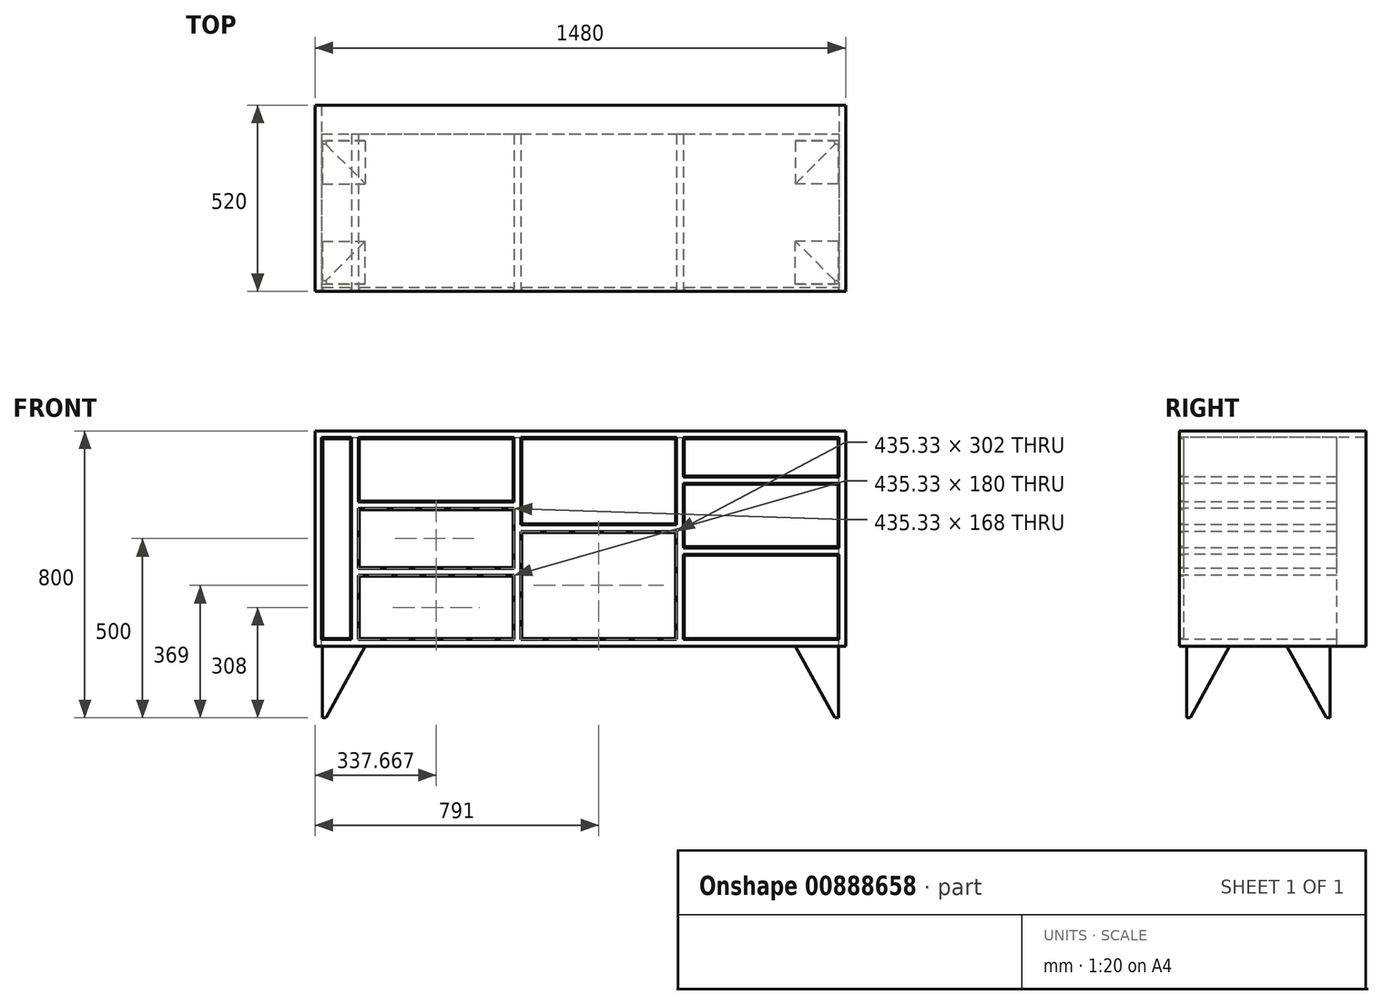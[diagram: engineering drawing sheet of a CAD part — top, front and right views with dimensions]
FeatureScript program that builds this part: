
annotation { "Feature Type Name" : "Feature", "Feature Type Description" : "" }
export const myFeature = defineFeature(function(context is Context, id is Id, definition is map)
    precondition{}
    {
        {
            assignVariable(context, id + "F0", {"name" : "depth", "anyValue" : 520});
        }
        {
            assignVariable(context, id + "F1", {"name" : "hollow_back", "anyValue" : 80});
        }
        {
            var Q0;
            Q0=qCreatedBy(makeId("Front.planeOp"),FACE);
            var sketch = newSketch(context, id + "F2", { "sketchPlane" : qUnion([Q0])});
            skLineSegment(sketch, "E0.bottom", {"start": v(0, 0) * mm, "end": v(1480, 0) * mm});
            skLineSegment(sketch, "E0.top", {"start": v(0, 600) * mm, "end": v(1480, 600) * mm});
            skLineSegment(sketch, "E0.left", {"start": v(0, 0) * mm, "end": v(0, 600) * mm});
            skLineSegment(sketch, "E0.right", {"start": v(1480, 0) * mm, "end": v(1480, 600) * mm});
            skLineSegment(sketch, "E1", {"start": v(120, 0) * mm, "end": v(120, 600) * mm});
            skLineSegment(sketch, "E2.0", {"start": v(102, 0) * mm, "end": v(102, 600) * mm});
            skLineSegment(sketch, "E3.0", {"start": v(18, 0) * mm, "end": v(18, 600) * mm});
            skLineSegment(sketch, "E4", {"start": v(564.33, 0) * mm, "end": v(564.33, 600) * mm});
            skLineSegment(sketch, "E5", {"start": v(1017.67, 0) * mm, "end": v(1017.67, 600) * mm});
            skLineSegment(sketch, "E6.0", {"start": v(573.33, 0) * mm, "end": v(573.33, 600) * mm});
            skLineSegment(sketch, "E7.0", {"start": v(555.33, 0) * mm, "end": v(555.33, 600) * mm});
            skLineSegment(sketch, "E8.0", {"start": v(1026.67, 0) * mm, "end": v(1026.67, 600) * mm});
            skLineSegment(sketch, "E9.0", {"start": v(1008.67, 0) * mm, "end": v(1008.67, 600) * mm});
            skLineSegment(sketch, "E10.0", {"start": v(0, 582) * mm, "end": v(1480, 582) * mm});
            skLineSegment(sketch, "E11.0", {"start": v(1462, 0) * mm, "end": v(1462, 600) * mm});
            skLineSegment(sketch, "E12.0", {"start": v(0, 18) * mm, "end": v(1480, 18) * mm});
            skLineSegment(sketch, "E13.0", {"start": v(111, 0) * mm, "end": v(111, 600) * mm});
            skLineSegment(sketch, "E14.0", {"start": v(1471, 0) * mm, "end": v(1471, 600) * mm});
            skLineSegment(sketch, "E15", {"start": v(573.33, 338) * mm, "end": v(1008.67, 338) * mm});
            skLineSegment(sketch, "E16.0", {"start": v(573.33, 320) * mm, "end": v(1008.67, 320) * mm});
            skLineSegment(sketch, "E17", {"start": v(120, 402) * mm, "end": v(555.33, 402) * mm});
            skLineSegment(sketch, "E18.0", {"start": v(120, 384) * mm, "end": v(555.33, 384) * mm});
            skLineSegment(sketch, "E19", {"start": v(120, 216) * mm, "end": v(555.33, 216) * mm});
            skLineSegment(sketch, "E20.0", {"start": v(120, 198) * mm, "end": v(555.33, 198) * mm});
            skLineSegment(sketch, "E21", {"start": v(1026.67, 472) * mm, "end": v(1462, 472) * mm});
            skLineSegment(sketch, "E22.0", {"start": v(1026.67, 454) * mm, "end": v(1462, 454) * mm});
            skLineSegment(sketch, "E23", {"start": v(1026.67, 274) * mm, "end": v(1462, 274) * mm});
            skLineSegment(sketch, "E24.0", {"start": v(1026.67, 256) * mm, "end": v(1462, 256) * mm});
            skSolve(sketch);
        }
        {
            var Q0;
            {var subQ0=sQuery(id+"F2.wireOp",EDGE,"E10.0");var subQ1=sQuery(id+"F2.wireOp",EDGE,"E0.left");var subQ2=makeQuery(id+"F2.imprint","INTERSECT",VERTEX,{"derivedFrom":[subQ1,subQ0]});Q0=makeQuery(id+"F2.imprint","IMPRINT",FACE,{"disambiguationData":[TD([[makeQuery(id+"F2.imprint","IMPRINT",EDGE,{"disambiguationData":[TD([[subQ2,1.0]])],"derivedFrom":subQ1}),-1.0]])]});}
            var Q1;
            {var subQ0=sQuery(id+"F2.wireOp",EDGE,"E0.left");var subQ1=sQuery(id+"F2.wireOp",EDGE,"E0.top");var subQ2=makeQuery(id+"F2.imprint","INTERSECT",VERTEX,{"derivedFrom":[subQ1,subQ0]});Q1=makeQuery(id+"F2.imprint","IMPRINT",FACE,{"disambiguationData":[TD([[makeQuery(id+"F2.imprint","IMPRINT",EDGE,{"disambiguationData":[TD([[subQ2,-1.0]])],"derivedFrom":subQ1}),-1.0]])]});}
            var Q2;
            {var subQ0=sQuery(id+"F2.wireOp",EDGE,"E2.0");var subQ1=sQuery(id+"F2.wireOp",EDGE,"E0.top");var subQ2=makeQuery(id+"F2.imprint","INTERSECT",VERTEX,{"derivedFrom":[subQ1,subQ0]});Q2=makeQuery(id+"F2.imprint","IMPRINT",FACE,{"disambiguationData":[TD([[makeQuery(id+"F2.imprint","IMPRINT",EDGE,{"disambiguationData":[TD([[subQ2,1.0]])],"derivedFrom":subQ1}),-1.0]])]});}
            var Q3;
            {var subQ0=sQuery(id+"F2.wireOp",EDGE,"E1");var subQ1=sQuery(id+"F2.wireOp",EDGE,"E0.top");var subQ2=makeQuery(id+"F2.imprint","INTERSECT",VERTEX,{"derivedFrom":[subQ1,subQ0]});Q3=makeQuery(id+"F2.imprint","IMPRINT",FACE,{"disambiguationData":[TD([[makeQuery(id+"F2.imprint","IMPRINT",EDGE,{"disambiguationData":[TD([[subQ2,1.0]])],"derivedFrom":subQ1}),-1.0]])]});}
            var Q4;
            {var subQ0=sQuery(id+"F2.wireOp",EDGE,"E1");var subQ1=sQuery(id+"F2.wireOp",EDGE,"E0.top");var subQ2=makeQuery(id+"F2.imprint","INTERSECT",VERTEX,{"derivedFrom":[subQ1,subQ0]});Q4=makeQuery(id+"F2.imprint","IMPRINT",FACE,{"disambiguationData":[TD([[makeQuery(id+"F2.imprint","IMPRINT",EDGE,{"disambiguationData":[TD([[subQ2,-1.0]])],"derivedFrom":subQ1}),-1.0]])]});}
            var Q5;
            {var subQ0=sQuery(id+"F2.wireOp",EDGE,"E4");var subQ1=sQuery(id+"F2.wireOp",EDGE,"E0.top");var subQ2=makeQuery(id+"F2.imprint","INTERSECT",VERTEX,{"derivedFrom":[subQ1,subQ0]});Q5=makeQuery(id+"F2.imprint","IMPRINT",FACE,{"disambiguationData":[TD([[makeQuery(id+"F2.imprint","IMPRINT",EDGE,{"disambiguationData":[TD([[subQ2,1.0]])],"derivedFrom":subQ1}),-1.0]])]});}
            var Q6;
            {var subQ0=sQuery(id+"F2.wireOp",EDGE,"E4");var subQ1=sQuery(id+"F2.wireOp",EDGE,"E0.top");var subQ2=makeQuery(id+"F2.imprint","INTERSECT",VERTEX,{"derivedFrom":[subQ1,subQ0]});Q6=makeQuery(id+"F2.imprint","IMPRINT",FACE,{"disambiguationData":[TD([[makeQuery(id+"F2.imprint","IMPRINT",EDGE,{"disambiguationData":[TD([[subQ2,-1.0]])],"derivedFrom":subQ1}),-1.0]])]});}
            var Q7;
            {var subQ0=sQuery(id+"F2.wireOp",EDGE,"E6.0");var subQ1=sQuery(id+"F2.wireOp",EDGE,"E0.top");var subQ2=makeQuery(id+"F2.imprint","INTERSECT",VERTEX,{"derivedFrom":[subQ1,subQ0]});Q7=makeQuery(id+"F2.imprint","IMPRINT",FACE,{"disambiguationData":[TD([[makeQuery(id+"F2.imprint","IMPRINT",EDGE,{"disambiguationData":[TD([[subQ2,-1.0]])],"derivedFrom":subQ1}),-1.0]])]});}
            var Q8;
            {var subQ0=sQuery(id+"F2.wireOp",EDGE,"E5");var subQ1=sQuery(id+"F2.wireOp",EDGE,"E0.top");var subQ2=makeQuery(id+"F2.imprint","INTERSECT",VERTEX,{"derivedFrom":[subQ1,subQ0]});Q8=makeQuery(id+"F2.imprint","IMPRINT",FACE,{"disambiguationData":[TD([[makeQuery(id+"F2.imprint","IMPRINT",EDGE,{"disambiguationData":[TD([[subQ2,1.0]])],"derivedFrom":subQ1}),-1.0]])]});}
            var Q9;
            {var subQ0=sQuery(id+"F2.wireOp",EDGE,"E5");var subQ1=sQuery(id+"F2.wireOp",EDGE,"E0.top");var subQ2=makeQuery(id+"F2.imprint","INTERSECT",VERTEX,{"derivedFrom":[subQ1,subQ0]});Q9=makeQuery(id+"F2.imprint","IMPRINT",FACE,{"disambiguationData":[TD([[makeQuery(id+"F2.imprint","IMPRINT",EDGE,{"disambiguationData":[TD([[subQ2,-1.0]])],"derivedFrom":subQ1}),-1.0]])]});}
            var Q10;
            {var subQ0=sQuery(id+"F2.wireOp",EDGE,"E8.0");var subQ1=sQuery(id+"F2.wireOp",EDGE,"E0.top");var subQ2=makeQuery(id+"F2.imprint","INTERSECT",VERTEX,{"derivedFrom":[subQ1,subQ0]});Q10=makeQuery(id+"F2.imprint","IMPRINT",FACE,{"disambiguationData":[TD([[makeQuery(id+"F2.imprint","IMPRINT",EDGE,{"disambiguationData":[TD([[subQ2,-1.0]])],"derivedFrom":subQ1}),-1.0]])]});}
            var Q11;
            {var subQ0=sQuery(id+"F2.wireOp",EDGE,"E0.right");var subQ1=sQuery(id+"F2.wireOp",EDGE,"E0.top");var subQ2=makeQuery(id+"F2.imprint","INTERSECT",VERTEX,{"derivedFrom":[subQ1,subQ0]});Q11=makeQuery(id+"F2.imprint","IMPRINT",FACE,{"disambiguationData":[TD([[makeQuery(id+"F2.imprint","IMPRINT",EDGE,{"disambiguationData":[TD([[subQ2,1.0]])],"derivedFrom":subQ1}),-1.0]])]});}
            var Q12;
            {var subQ0=sQuery(id+"F2.wireOp",EDGE,"E10.0");var subQ1=sQuery(id+"F2.wireOp",EDGE,"E0.right");var subQ2=makeQuery(id+"F2.imprint","INTERSECT",VERTEX,{"derivedFrom":[subQ1,subQ0]});Q12=makeQuery(id+"F2.imprint","IMPRINT",FACE,{"disambiguationData":[TD([[makeQuery(id+"F2.imprint","IMPRINT",EDGE,{"disambiguationData":[TD([[subQ2,1.0]])],"derivedFrom":subQ1}),1.0]])]});}
            var Q13;
            {var subQ0=sQuery(id+"F2.wireOp",EDGE,"E0.right");var subQ1=sQuery(id+"F2.wireOp",EDGE,"E0.bottom");var subQ2=makeQuery(id+"F2.imprint","INTERSECT",VERTEX,{"derivedFrom":[subQ1,subQ0]});Q13=makeQuery(id+"F2.imprint","IMPRINT",FACE,{"disambiguationData":[TD([[makeQuery(id+"F2.imprint","IMPRINT",EDGE,{"disambiguationData":[TD([[subQ2,1.0]])],"derivedFrom":subQ1}),1.0]])]});}
            var Q14;
            {var subQ0=sQuery(id+"F2.wireOp",EDGE,"E0.left");var subQ1=sQuery(id+"F2.wireOp",EDGE,"E0.bottom");var subQ2=makeQuery(id+"F2.imprint","INTERSECT",VERTEX,{"derivedFrom":[subQ1,subQ0]});Q14=makeQuery(id+"F2.imprint","IMPRINT",FACE,{"disambiguationData":[TD([[makeQuery(id+"F2.imprint","IMPRINT",EDGE,{"disambiguationData":[TD([[subQ2,-1.0]])],"derivedFrom":subQ1}),1.0]])]});}
            var Q15;
            {var subQ0=sQuery(id+"F2.wireOp",EDGE,"E2.0");var subQ1=sQuery(id+"F2.wireOp",EDGE,"E0.top");var subQ2=makeQuery(id+"F2.imprint","INTERSECT",VERTEX,{"derivedFrom":[subQ1,subQ0]});Q15=makeQuery(id+"F2.imprint","IMPRINT",FACE,{"disambiguationData":[TD([[makeQuery(id+"F2.imprint","IMPRINT",EDGE,{"disambiguationData":[TD([[subQ2,-1.0]])],"derivedFrom":subQ1}),-1.0]])]});}
            var Q16;
            {var subQ0=sQuery(id+"F2.wireOp",EDGE,"E11.0");var subQ1=sQuery(id+"F2.wireOp",EDGE,"E0.top");var subQ2=makeQuery(id+"F2.imprint","INTERSECT",VERTEX,{"derivedFrom":[subQ1,subQ0]});Q16=makeQuery(id+"F2.imprint","IMPRINT",FACE,{"disambiguationData":[TD([[makeQuery(id+"F2.imprint","IMPRINT",EDGE,{"disambiguationData":[TD([[subQ2,-1.0]])],"derivedFrom":subQ1}),-1.0]])]});}
            var Q17;
            {var subQ0=sQuery(id+"F2.wireOp",EDGE,"E11.0");var subQ1=sQuery(id+"F2.wireOp",EDGE,"E10.0");var subQ2=makeQuery(id+"F2.imprint","INTERSECT",VERTEX,{"derivedFrom":[subQ1,subQ0]});Q17=makeQuery(id+"F2.imprint","IMPRINT",FACE,{"disambiguationData":[TD([[makeQuery(id+"F2.imprint","IMPRINT",EDGE,{"disambiguationData":[TD([[subQ2,-1.0]])],"derivedFrom":subQ1}),-1.0]])]});}
            var Q18;
            {var subQ0=sQuery(id+"F2.wireOp",EDGE,"E11.0");var subQ1=sQuery(id+"F2.wireOp",EDGE,"E0.bottom");var subQ2=makeQuery(id+"F2.imprint","INTERSECT",VERTEX,{"derivedFrom":[subQ1,subQ0]});Q18=makeQuery(id+"F2.imprint","IMPRINT",FACE,{"disambiguationData":[TD([[makeQuery(id+"F2.imprint","IMPRINT",EDGE,{"disambiguationData":[TD([[subQ2,-1.0]])],"derivedFrom":subQ1}),1.0]])]});}
            extrude(context, id + "F3", {"entities" : qUnion([Q0, Q1, Q2, Q3, Q4, Q5, Q6, Q7, Q8, Q9, Q10, Q11, Q12, Q13, Q14, Q15, Q16, Q17, Q18]), "oppositeDirection" : true, "depth" : (getVariable(context, 'depth')) * mm, "offsetDistance" : 25 * mm});
        }
        {
            var Q0;
            {var subQ0=sQuery(id+"F2.wireOp",EDGE,"E8.0");var subQ1=sQuery(id+"F2.wireOp",EDGE,"E0.bottom");var subQ2=makeQuery(id+"F2.imprint","INTERSECT",VERTEX,{"derivedFrom":[subQ1,subQ0]});Q0=makeQuery(id+"F2.imprint","IMPRINT",FACE,{"disambiguationData":[TD([[makeQuery(id+"F2.imprint","IMPRINT",EDGE,{"disambiguationData":[TD([[subQ2,-1.0]])],"derivedFrom":subQ1}),1.0]])]});}
            var Q1;
            {var subQ0=sQuery(id+"F2.wireOp",EDGE,"E5");var subQ1=sQuery(id+"F2.wireOp",EDGE,"E0.bottom");var subQ2=makeQuery(id+"F2.imprint","INTERSECT",VERTEX,{"derivedFrom":[subQ1,subQ0]});Q1=makeQuery(id+"F2.imprint","IMPRINT",FACE,{"disambiguationData":[TD([[makeQuery(id+"F2.imprint","IMPRINT",EDGE,{"disambiguationData":[TD([[subQ2,-1.0]])],"derivedFrom":subQ1}),1.0]])]});}
            var Q2;
            {var subQ0=sQuery(id+"F2.wireOp",EDGE,"E5");var subQ1=sQuery(id+"F2.wireOp",EDGE,"E0.bottom");var subQ2=makeQuery(id+"F2.imprint","INTERSECT",VERTEX,{"derivedFrom":[subQ1,subQ0]});Q2=makeQuery(id+"F2.imprint","IMPRINT",FACE,{"disambiguationData":[TD([[makeQuery(id+"F2.imprint","IMPRINT",EDGE,{"disambiguationData":[TD([[subQ2,1.0]])],"derivedFrom":subQ1}),1.0]])]});}
            var Q3;
            {var subQ0=sQuery(id+"F2.wireOp",EDGE,"E6.0");var subQ1=sQuery(id+"F2.wireOp",EDGE,"E0.bottom");var subQ2=makeQuery(id+"F2.imprint","INTERSECT",VERTEX,{"derivedFrom":[subQ1,subQ0]});Q3=makeQuery(id+"F2.imprint","IMPRINT",FACE,{"disambiguationData":[TD([[makeQuery(id+"F2.imprint","IMPRINT",EDGE,{"disambiguationData":[TD([[subQ2,-1.0]])],"derivedFrom":subQ1}),1.0]])]});}
            var Q4;
            {var subQ0=sQuery(id+"F2.wireOp",EDGE,"E4");var subQ1=sQuery(id+"F2.wireOp",EDGE,"E0.bottom");var subQ2=makeQuery(id+"F2.imprint","INTERSECT",VERTEX,{"derivedFrom":[subQ1,subQ0]});Q4=makeQuery(id+"F2.imprint","IMPRINT",FACE,{"disambiguationData":[TD([[makeQuery(id+"F2.imprint","IMPRINT",EDGE,{"disambiguationData":[TD([[subQ2,-1.0]])],"derivedFrom":subQ1}),1.0]])]});}
            var Q5;
            {var subQ0=sQuery(id+"F2.wireOp",EDGE,"E4");var subQ1=sQuery(id+"F2.wireOp",EDGE,"E0.bottom");var subQ2=makeQuery(id+"F2.imprint","INTERSECT",VERTEX,{"derivedFrom":[subQ1,subQ0]});Q5=makeQuery(id+"F2.imprint","IMPRINT",FACE,{"disambiguationData":[TD([[makeQuery(id+"F2.imprint","IMPRINT",EDGE,{"disambiguationData":[TD([[subQ2,1.0]])],"derivedFrom":subQ1}),1.0]])]});}
            var Q6;
            {var subQ0=sQuery(id+"F2.wireOp",EDGE,"E1");var subQ1=sQuery(id+"F2.wireOp",EDGE,"E0.bottom");var subQ2=makeQuery(id+"F2.imprint","INTERSECT",VERTEX,{"derivedFrom":[subQ1,subQ0]});Q6=makeQuery(id+"F2.imprint","IMPRINT",FACE,{"disambiguationData":[TD([[makeQuery(id+"F2.imprint","IMPRINT",EDGE,{"disambiguationData":[TD([[subQ2,-1.0]])],"derivedFrom":subQ1}),1.0]])]});}
            var Q7;
            {var subQ0=sQuery(id+"F2.wireOp",EDGE,"E1");var subQ1=sQuery(id+"F2.wireOp",EDGE,"E0.bottom");var subQ2=makeQuery(id+"F2.imprint","INTERSECT",VERTEX,{"derivedFrom":[subQ1,subQ0]});Q7=makeQuery(id+"F2.imprint","IMPRINT",FACE,{"disambiguationData":[TD([[makeQuery(id+"F2.imprint","IMPRINT",EDGE,{"disambiguationData":[TD([[subQ2,1.0]])],"derivedFrom":subQ1}),1.0]])]});}
            var Q8;
            {var subQ0=sQuery(id+"F2.wireOp",EDGE,"E2.0");var subQ1=sQuery(id+"F2.wireOp",EDGE,"E0.bottom");var subQ2=makeQuery(id+"F2.imprint","INTERSECT",VERTEX,{"derivedFrom":[subQ1,subQ0]});Q8=makeQuery(id+"F2.imprint","IMPRINT",FACE,{"disambiguationData":[TD([[makeQuery(id+"F2.imprint","IMPRINT",EDGE,{"disambiguationData":[TD([[subQ2,1.0]])],"derivedFrom":subQ1}),1.0]])]});}
            var Q9;
            {var subQ0=sQuery(id+"F2.wireOp",EDGE,"E12.0");var subQ1=sQuery(id+"F2.wireOp",EDGE,"E1");var subQ2=makeQuery(id+"F2.imprint","INTERSECT",VERTEX,{"derivedFrom":[subQ1,subQ0]});Q9=makeQuery(id+"F2.imprint","IMPRINT",FACE,{"disambiguationData":[TD([[makeQuery(id+"F2.imprint","IMPRINT",EDGE,{"disambiguationData":[TD([[subQ2,-1.0]])],"derivedFrom":subQ1}),1.0]])]});}
            var Q10;
            {var subQ0=sQuery(id+"F2.wireOp",EDGE,"E12.0");var subQ1=sQuery(id+"F2.wireOp",EDGE,"E4");var subQ2=makeQuery(id+"F2.imprint","INTERSECT",VERTEX,{"derivedFrom":[subQ1,subQ0]});Q10=makeQuery(id+"F2.imprint","IMPRINT",FACE,{"disambiguationData":[TD([[makeQuery(id+"F2.imprint","IMPRINT",EDGE,{"disambiguationData":[TD([[subQ2,-1.0]])],"derivedFrom":subQ1}),1.0]])]});}
            var Q11;
            {var subQ0=sQuery(id+"F2.wireOp",EDGE,"E12.0");var subQ1=sQuery(id+"F2.wireOp",EDGE,"E4");var subQ2=makeQuery(id+"F2.imprint","INTERSECT",VERTEX,{"derivedFrom":[subQ1,subQ0]});Q11=makeQuery(id+"F2.imprint","IMPRINT",FACE,{"disambiguationData":[TD([[makeQuery(id+"F2.imprint","IMPRINT",EDGE,{"disambiguationData":[TD([[subQ2,-1.0]])],"derivedFrom":subQ1}),-1.0]])]});}
            var Q12;
            {var subQ0=sQuery(id+"F2.wireOp",EDGE,"E12.0");var subQ1=sQuery(id+"F2.wireOp",EDGE,"E5");var subQ2=makeQuery(id+"F2.imprint","INTERSECT",VERTEX,{"derivedFrom":[subQ1,subQ0]});Q12=makeQuery(id+"F2.imprint","IMPRINT",FACE,{"disambiguationData":[TD([[makeQuery(id+"F2.imprint","IMPRINT",EDGE,{"disambiguationData":[TD([[subQ2,-1.0]])],"derivedFrom":subQ1}),1.0]])]});}
            var Q13;
            {var subQ0=sQuery(id+"F2.wireOp",EDGE,"E12.0");var subQ1=sQuery(id+"F2.wireOp",EDGE,"E5");var subQ2=makeQuery(id+"F2.imprint","INTERSECT",VERTEX,{"derivedFrom":[subQ1,subQ0]});Q13=makeQuery(id+"F2.imprint","IMPRINT",FACE,{"disambiguationData":[TD([[makeQuery(id+"F2.imprint","IMPRINT",EDGE,{"disambiguationData":[TD([[subQ2,-1.0]])],"derivedFrom":subQ1}),-1.0]])]});}
            var Q14;
            {var subQ0=sQuery(id+"F2.wireOp",EDGE,"E2.0");var subQ1=sQuery(id+"F2.wireOp",EDGE,"E0.bottom");var subQ2=makeQuery(id+"F2.imprint","INTERSECT",VERTEX,{"derivedFrom":[subQ1,subQ0]});Q14=makeQuery(id+"F2.imprint","IMPRINT",FACE,{"disambiguationData":[TD([[makeQuery(id+"F2.imprint","IMPRINT",EDGE,{"disambiguationData":[TD([[subQ2,-1.0]])],"derivedFrom":subQ1}),1.0]])]});}
            var Q15;
            {var subQ0=sQuery(id+"F2.wireOp",EDGE,"E12.0");var subQ1=sQuery(id+"F2.wireOp",EDGE,"E2.0");var subQ2=makeQuery(id+"F2.imprint","INTERSECT",VERTEX,{"derivedFrom":[subQ1,subQ0]});Q15=makeQuery(id+"F2.imprint","IMPRINT",FACE,{"disambiguationData":[TD([[makeQuery(id+"F2.imprint","IMPRINT",EDGE,{"disambiguationData":[TD([[subQ2,-1.0]])],"derivedFrom":subQ1}),-1.0]])]});}
            var Q16;
            {var subQ0=sQuery(id+"F2.wireOp",EDGE,"E17");Q16=makeQuery(id+"F2.imprint","IMPRINT",FACE,{"disambiguationData":[TD([[makeQuery(id+"F2.imprint","IMPRINT",EDGE,{"derivedFrom":subQ0}),-1.0]])]});}
            var Q17;
            {var subQ0=sQuery(id+"F2.wireOp",EDGE,"E19");Q17=makeQuery(id+"F2.imprint","IMPRINT",FACE,{"disambiguationData":[TD([[makeQuery(id+"F2.imprint","IMPRINT",EDGE,{"derivedFrom":subQ0}),-1.0]])]});}
            var Q18;
            {var subQ0=sQuery(id+"F2.wireOp",EDGE,"E15");Q18=makeQuery(id+"F2.imprint","IMPRINT",FACE,{"disambiguationData":[TD([[makeQuery(id+"F2.imprint","IMPRINT",EDGE,{"derivedFrom":subQ0}),-1.0]])]});}
            var Q19;
            {var subQ0=sQuery(id+"F2.wireOp",EDGE,"E21");Q19=makeQuery(id+"F2.imprint","IMPRINT",FACE,{"disambiguationData":[TD([[makeQuery(id+"F2.imprint","IMPRINT",EDGE,{"derivedFrom":subQ0}),-1.0]])]});}
            var Q20;
            {var subQ0=sQuery(id+"F2.wireOp",EDGE,"E23");Q20=makeQuery(id+"F2.imprint","IMPRINT",FACE,{"disambiguationData":[TD([[makeQuery(id+"F2.imprint","IMPRINT",EDGE,{"derivedFrom":subQ0}),-1.0]])]});}
            extrude(context, id + "F4", {"entities" : qUnion([Q0, Q1, Q2, Q3, Q4, Q5, Q6, Q7, Q8, Q9, Q10, Q11, Q12, Q13, Q14, Q15, Q16, Q17, Q18, Q19, Q20]), "operationType" : NewBodyOperationType.ADD, "oppositeDirection" : true, "depth" : (getVariable(context, 'depth') - getVariable(context, 'hollow_back')) * mm, "offsetDistance" : 25 * mm});
        }
        {
            var Q0;
            Q0=qCreatedBy(makeId("Front.planeOp"),FACE);
            var sketch = newSketch(context, id + "F5", { "sketchPlane" : qUnion([Q0])});
            skLineSegment(sketch, "E25.0", {"start": v(21, 0) * mm, "end": v(21, 600) * mm});
            skLineSegment(sketch, "E26.0", {"start": v(0, 21) * mm, "end": v(1480, 21) * mm});
            skLineSegment(sketch, "E27.0", {"start": v(99, 0) * mm, "end": v(99, 600) * mm});
            skLineSegment(sketch, "E28.0", {"start": v(0, 579) * mm, "end": v(1480, 579) * mm});
            skLineSegment(sketch, "E29.0", {"start": v(123, 0) * mm, "end": v(123, 600) * mm});
            skLineSegment(sketch, "E30.0", {"start": v(552.33, 0) * mm, "end": v(552.33, 600) * mm});
            skLineSegment(sketch, "E31.0", {"start": v(120, 405) * mm, "end": v(555.33, 405) * mm});
            skLineSegment(sketch, "E32.0", {"start": v(120, 381) * mm, "end": v(555.33, 381) * mm});
            skLineSegment(sketch, "E33.0", {"start": v(120, 219) * mm, "end": v(555.33, 219) * mm});
            skLineSegment(sketch, "E34.0", {"start": v(120, 195) * mm, "end": v(555.33, 195) * mm});
            skLineSegment(sketch, "E35.0", {"start": v(576.33, 0) * mm, "end": v(576.33, 600) * mm});
            skLineSegment(sketch, "E36.0", {"start": v(1005.67, 0) * mm, "end": v(1005.67, 600) * mm});
            skLineSegment(sketch, "E37.0", {"start": v(573.33, 341) * mm, "end": v(1008.67, 341) * mm});
            skLineSegment(sketch, "E38.0", {"start": v(573.33, 317) * mm, "end": v(1008.67, 317) * mm});
            skLineSegment(sketch, "E39.0", {"start": v(1029.67, 0) * mm, "end": v(1029.67, 600) * mm});
            skLineSegment(sketch, "E40.0", {"start": v(1459, 0) * mm, "end": v(1459, 600) * mm});
            skLineSegment(sketch, "E41.0", {"start": v(1026.67, 475) * mm, "end": v(1462, 475) * mm});
            skLineSegment(sketch, "E42.0", {"start": v(1026.67, 451) * mm, "end": v(1462, 451) * mm});
            skLineSegment(sketch, "E43.0", {"start": v(1026.67, 277) * mm, "end": v(1462, 277) * mm});
            skLineSegment(sketch, "E44.0", {"start": v(1026.67, 253) * mm, "end": v(1462, 253) * mm});
            skSolve(sketch);
        }
        {
            var Q0;
            {var subQ0=sQuery(id+"F5.wireOp",EDGE,"E26.0");var subQ1=sQuery(id+"F5.wireOp",EDGE,"E25.0");var subQ2=makeQuery(id+"F5.imprint","INTERSECT",VERTEX,{"derivedFrom":[subQ1,subQ0]});Q0=makeQuery(id+"F5.imprint","IMPRINT",FACE,{"disambiguationData":[TD([[makeQuery(id+"F5.imprint","IMPRINT",EDGE,{"disambiguationData":[TD([[subQ2,-1.0]])],"derivedFrom":subQ1}),-1.0]])]});}
            var Q1;
            {var subQ0=sQuery(id+"F5.wireOp",EDGE,"E30.0");var subQ1=sQuery(id+"F5.wireOp",EDGE,"E28.0");var subQ2=makeQuery(id+"F5.imprint","INTERSECT",VERTEX,{"derivedFrom":[subQ1,subQ0]});Q1=makeQuery(id+"F5.imprint","IMPRINT",FACE,{"disambiguationData":[TD([[makeQuery(id+"F5.imprint","IMPRINT",EDGE,{"disambiguationData":[TD([[subQ2,1.0]])],"derivedFrom":subQ1}),-1.0]])]});}
            var Q2;
            {var subQ0=sQuery(id+"F5.wireOp",EDGE,"E33.0");var subQ1=sQuery(id+"F5.wireOp",EDGE,"E29.0");var subQ2=makeQuery(id+"F5.imprint","INTERSECT",VERTEX,{"derivedFrom":[subQ1,subQ0]});Q2=makeQuery(id+"F5.imprint","IMPRINT",FACE,{"disambiguationData":[TD([[makeQuery(id+"F5.imprint","IMPRINT",EDGE,{"disambiguationData":[TD([[subQ2,-1.0]])],"derivedFrom":subQ1}),-1.0]])]});}
            var Q3;
            {var subQ0=sQuery(id+"F5.wireOp",EDGE,"E29.0");var subQ1=sQuery(id+"F5.wireOp",EDGE,"E26.0");var subQ2=makeQuery(id+"F5.imprint","INTERSECT",VERTEX,{"derivedFrom":[subQ1,subQ0]});Q3=makeQuery(id+"F5.imprint","IMPRINT",FACE,{"disambiguationData":[TD([[makeQuery(id+"F5.imprint","IMPRINT",EDGE,{"disambiguationData":[TD([[subQ2,-1.0]])],"derivedFrom":subQ1}),1.0]])]});}
            var Q4;
            {var subQ0=sQuery(id+"F5.wireOp",EDGE,"E36.0");var subQ1=sQuery(id+"F5.wireOp",EDGE,"E28.0");var subQ2=makeQuery(id+"F5.imprint","INTERSECT",VERTEX,{"derivedFrom":[subQ1,subQ0]});Q4=makeQuery(id+"F5.imprint","IMPRINT",FACE,{"disambiguationData":[TD([[makeQuery(id+"F5.imprint","IMPRINT",EDGE,{"disambiguationData":[TD([[subQ2,1.0]])],"derivedFrom":subQ1}),-1.0]])]});}
            var Q5;
            {var subQ0=sQuery(id+"F5.wireOp",EDGE,"E36.0");var subQ1=sQuery(id+"F5.wireOp",EDGE,"E26.0");var subQ2=makeQuery(id+"F5.imprint","INTERSECT",VERTEX,{"derivedFrom":[subQ1,subQ0]});Q5=makeQuery(id+"F5.imprint","IMPRINT",FACE,{"disambiguationData":[TD([[makeQuery(id+"F5.imprint","IMPRINT",EDGE,{"disambiguationData":[TD([[subQ2,1.0]])],"derivedFrom":subQ1}),1.0]])]});}
            var Q6;
            {var subQ0=sQuery(id+"F5.wireOp",EDGE,"E40.0");var subQ1=sQuery(id+"F5.wireOp",EDGE,"E26.0");var subQ2=makeQuery(id+"F5.imprint","INTERSECT",VERTEX,{"derivedFrom":[subQ1,subQ0]});Q6=makeQuery(id+"F5.imprint","IMPRINT",FACE,{"disambiguationData":[TD([[makeQuery(id+"F5.imprint","IMPRINT",EDGE,{"disambiguationData":[TD([[subQ2,1.0]])],"derivedFrom":subQ1}),1.0]])]});}
            var Q7;
            {var subQ0=sQuery(id+"F5.wireOp",EDGE,"E43.0");var subQ1=sQuery(id+"F5.wireOp",EDGE,"E39.0");var subQ2=makeQuery(id+"F5.imprint","INTERSECT",VERTEX,{"derivedFrom":[subQ1,subQ0]});Q7=makeQuery(id+"F5.imprint","IMPRINT",FACE,{"disambiguationData":[TD([[makeQuery(id+"F5.imprint","IMPRINT",EDGE,{"disambiguationData":[TD([[subQ2,-1.0]])],"derivedFrom":subQ1}),-1.0]])]});}
            var Q8;
            {var subQ0=sQuery(id+"F5.wireOp",EDGE,"E40.0");var subQ1=sQuery(id+"F5.wireOp",EDGE,"E28.0");var subQ2=makeQuery(id+"F5.imprint","INTERSECT",VERTEX,{"derivedFrom":[subQ1,subQ0]});Q8=makeQuery(id+"F5.imprint","IMPRINT",FACE,{"disambiguationData":[TD([[makeQuery(id+"F5.imprint","IMPRINT",EDGE,{"disambiguationData":[TD([[subQ2,1.0]])],"derivedFrom":subQ1}),-1.0]])]});}
            extrude(context, id + "F6", {"entities" : qUnion([Q0, Q1, Q2, Q3, Q4, Q5, Q6, Q7, Q8]), "operationType" : NewBodyOperationType.ADD, "oppositeDirection" : true, "depth" : 12 * mm, "offsetDistance" : 25 * mm});
        }
        {
            var Q0;
            {var subQ0=sQuery(id+"F2.wireOp",EDGE,"E0.bottom");Q0=makeQuery(id+"F4.boolean.opBoolean","MERGE",FACE,{"derivedFrom":[makeQuery(id+"F3.opExtrude","SWEPT_FACE",FACE,{"disambiguationData":[OSD([subQ0]),TDD([makeQuery(id+"F2.imprint","IMPRINT",EDGE,{"disambiguationData":[TD([[makeQuery(id+"F2.imprint","INTERSECT",VERTEX,{"derivedFrom":[subQ0,sQuery(id+"F2.wireOp",EDGE,"E0.left")]}),-1.0]])],"derivedFrom":subQ0})])]}),makeQuery(id+"F3.opExtrude","SWEPT_FACE",FACE,{"disambiguationData":[OSD([subQ0]),TDD([makeQuery(id+"F2.imprint","IMPRINT",EDGE,{"disambiguationData":[TD([[makeQuery(id+"F2.imprint","INTERSECT",VERTEX,{"derivedFrom":[subQ0,sQuery(id+"F2.wireOp",EDGE,"E11.0")]}),-1.0]])],"derivedFrom":subQ0}),makeQuery(id+"F2.imprint","IMPRINT",EDGE,{"disambiguationData":[TD([[makeQuery(id+"F2.imprint","INTERSECT",VERTEX,{"derivedFrom":[subQ0,sQuery(id+"F2.wireOp",EDGE,"E0.right")]}),1.0]])],"derivedFrom":subQ0})])]}),makeQuery(id+"F4.opExtrude","SWEPT_FACE",FACE,{"disambiguationData":[OSD([subQ0])]})]});}
            var sketch = newSketch(context, id + "F7", { "sketchPlane" : qUnion([Q0])});
            skLineSegment(sketch, "E45.bottom", {"start": v(20, -20) * mm, "end": v(140, -20) * mm});
            skLineSegment(sketch, "E45.top", {"start": v(20, -140) * mm, "end": v(140, -140) * mm});
            skLineSegment(sketch, "E45.left", {"start": v(20, -20) * mm, "end": v(20, -140) * mm});
            skLineSegment(sketch, "E45.right", {"start": v(140, -20) * mm, "end": v(140, -140) * mm});
            skLineSegment(sketch, "E46", {"start": v(740, 0) * mm, "end": v(740, -440) * mm, "construction": true});
            skLineSegment(sketch, "E47", {"start": v(740, -220) * mm, "end": v(1480, -220) * mm, "construction": true});
            skLineSegment(sketch, "E48.MirrorCS", {"start": v(1340, -20) * mm, "end": v(1340, -140) * mm});
            skLineSegment(sketch, "E49.MirrorCS", {"start": v(1460, -140) * mm, "end": v(1340, -140) * mm});
            skLineSegment(sketch, "E50.MirrorCS", {"start": v(1460, -20) * mm, "end": v(1460, -140) * mm});
            skLineSegment(sketch, "E51.MirrorCS", {"start": v(1460, -20) * mm, "end": v(1340, -20) * mm});
            skLineSegment(sketch, "E52.MirrorCS", {"start": v(1460, -300) * mm, "end": v(1340, -300) * mm});
            skLineSegment(sketch, "E53.MirrorCS", {"start": v(1340, -420) * mm, "end": v(1340, -300) * mm});
            skLineSegment(sketch, "E54.MirrorCS", {"start": v(1460, -420) * mm, "end": v(1340, -420) * mm});
            skLineSegment(sketch, "E55.MirrorCS", {"start": v(1460, -420) * mm, "end": v(1460, -300) * mm});
            skLineSegment(sketch, "E56.MirrorCS", {"start": v(140, -420) * mm, "end": v(140, -300) * mm});
            skLineSegment(sketch, "E57.MirrorCS", {"start": v(20, -420) * mm, "end": v(140, -420) * mm});
            skLineSegment(sketch, "E58.MirrorCS", {"start": v(20, -420) * mm, "end": v(20, -300) * mm});
            skLineSegment(sketch, "E59.MirrorCS", {"start": v(20, -300) * mm, "end": v(140, -300) * mm});
            skSolve(sketch);
        }
        {
            var Q0;
            Q0=makeQuery(id+"F7.imprint","IMPRINT",FACE,{"disambiguationData":[TD([[makeQuery(id+"F7.imprint","IMPRINT",EDGE,{"derivedFrom":sQuery(id+"F7.wireOp",EDGE,"E45.bottom")}),-1.0]])]});
            var Q1;
            Q1=makeQuery(id+"F7.imprint","IMPRINT",FACE,{"disambiguationData":[TD([[makeQuery(id+"F7.imprint","IMPRINT",EDGE,{"derivedFrom":sQuery(id+"F7.wireOp",EDGE,"E48.MirrorCS")}),1.0]])]});
            var Q2;
            Q2=makeQuery(id+"F7.imprint","IMPRINT",FACE,{"disambiguationData":[TD([[makeQuery(id+"F7.imprint","IMPRINT",EDGE,{"derivedFrom":sQuery(id+"F7.wireOp",EDGE,"E56.MirrorCS")}),1.0]])]});
            var Q3;
            Q3=makeQuery(id+"F7.imprint","IMPRINT",FACE,{"disambiguationData":[TD([[makeQuery(id+"F7.imprint","IMPRINT",EDGE,{"derivedFrom":sQuery(id+"F7.wireOp",EDGE,"E52.MirrorCS")}),1.0]])]});
            extrude(context, id + "F8", {"entities" : qUnion([Q0, Q1, Q2, Q3]), "operationType" : NewBodyOperationType.ADD, "depth" : 200 * mm, "offsetDistance" : 25 * mm});
        }
        {
            var Q0;
            Q0=makeQuery(id+"F8.opExtrude","CAP_EDGE",EDGE,{"disambiguationData":[OSD([sQuery(id+"F7.wireOp",EDGE,"E45.right")])],"isStart":false});
            var Q1;
            Q1=makeQuery(id+"F8.opExtrude","CAP_EDGE",EDGE,{"disambiguationData":[OSD([sQuery(id+"F7.wireOp",EDGE,"E53.MirrorCS")])],"isStart":false});
            chamfer(context, id + "F9", {"entities" : qUnion([Q0, Q1]), "chamferType" : ChamferType.TWO_OFFSETS, "width1" : 200 * mm, "oppositeDirection" : false, "width2" : 110 * mm, "tangentPropagation" : true});
        }
        {
            var Q0;
            Q0=makeQuery(id+"F8.opExtrude","CAP_EDGE",EDGE,{"disambiguationData":[OSD([sQuery(id+"F7.wireOp",EDGE,"E45.top")])],"isStart":false});
            var Q1;
            Q1=makeQuery(id+"F8.opExtrude","CAP_EDGE",EDGE,{"disambiguationData":[OSD([sQuery(id+"F7.wireOp",EDGE,"E52.MirrorCS")])],"isStart":false});
            chamfer(context, id + "F10", {"entities" : qUnion([Q0, Q1]), "chamferType" : ChamferType.TWO_OFFSETS, "width1" : 110 * mm, "oppositeDirection" : false, "width2" : 200 * mm, "tangentPropagation" : true});
        }
        {
            var Q0;
            Q0=makeQuery(id+"F8.opExtrude","CAP_EDGE",EDGE,{"disambiguationData":[OSD([sQuery(id+"F7.wireOp",EDGE,"E56.MirrorCS")])],"isStart":false});
            var Q1;
            Q1=makeQuery(id+"F8.opExtrude","CAP_EDGE",EDGE,{"disambiguationData":[OSD([sQuery(id+"F7.wireOp",EDGE,"E48.MirrorCS")])],"isStart":false});
            chamfer(context, id + "F11", {"entities" : qUnion([Q0, Q1]), "chamferType" : ChamferType.TWO_OFFSETS, "width1" : 200 * mm, "oppositeDirection" : true, "width2" : 110 * mm, "tangentPropagation" : true});
        }
        {
            var Q0;
            Q0=makeQuery(id+"F8.opExtrude","CAP_EDGE",EDGE,{"disambiguationData":[OSD([sQuery(id+"F7.wireOp",EDGE,"E59.MirrorCS")])],"isStart":false});
            var Q1;
            Q1=makeQuery(id+"F8.opExtrude","CAP_EDGE",EDGE,{"disambiguationData":[OSD([sQuery(id+"F7.wireOp",EDGE,"E49.MirrorCS")])],"isStart":false});
            chamfer(context, id + "F12", {"entities" : qUnion([Q0, Q1]), "chamferType" : ChamferType.TWO_OFFSETS, "width1" : 200 * mm, "oppositeDirection" : false, "width2" : 110 * mm, "tangentPropagation" : true});
        }
    });
